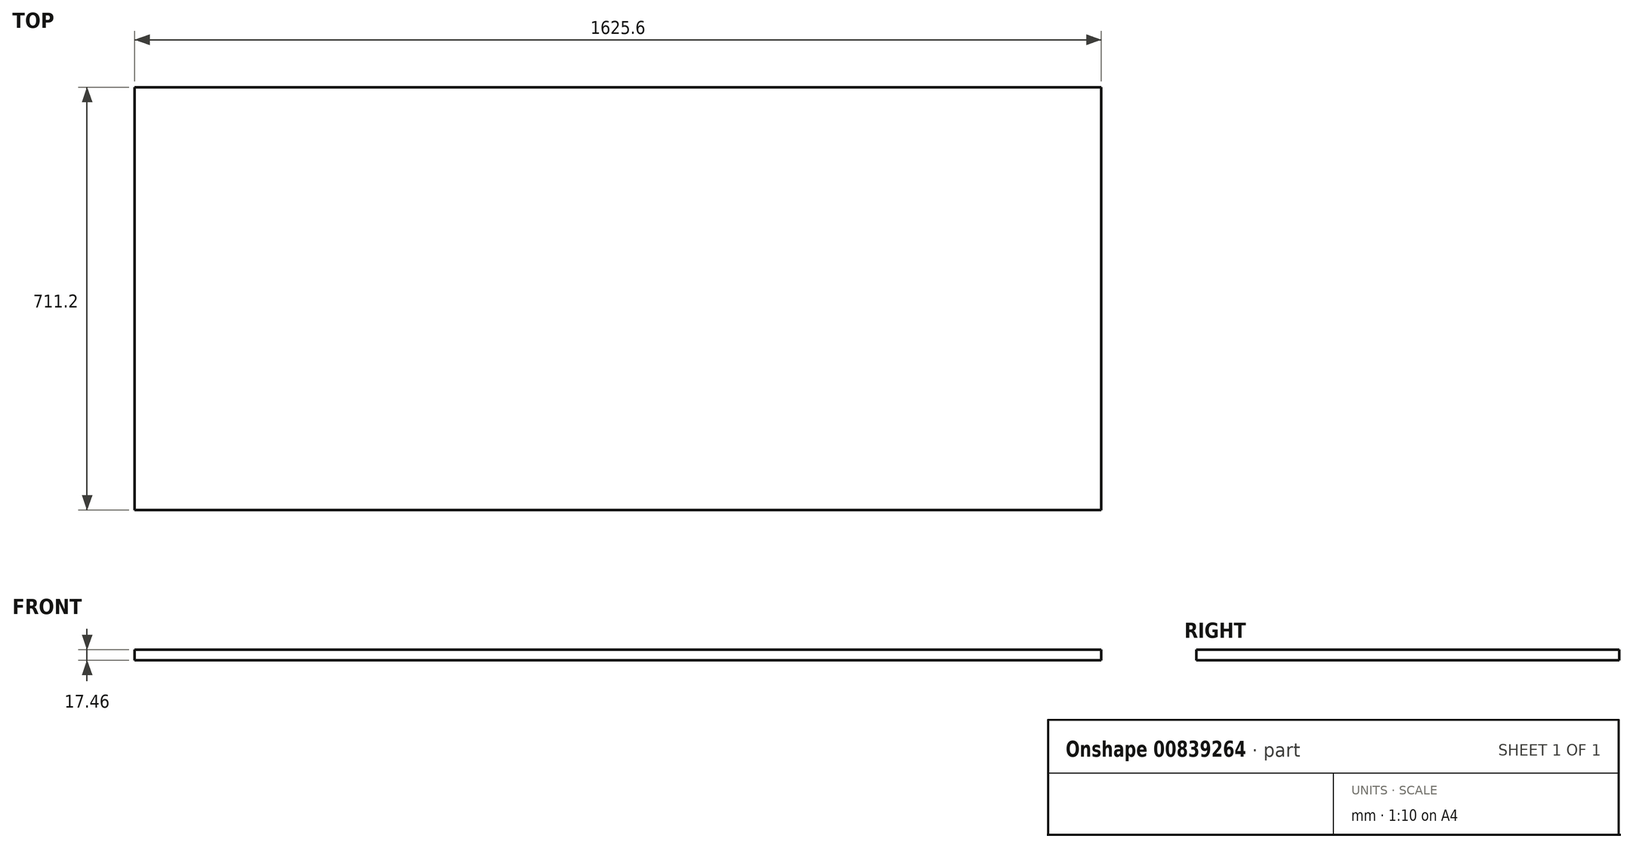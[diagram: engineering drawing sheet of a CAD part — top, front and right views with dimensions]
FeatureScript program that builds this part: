
annotation { "Feature Type Name" : "Feature", "Feature Type Description" : "" }
export const myFeature = defineFeature(function(context is Context, id is Id, definition is map)
    precondition{}
    {
        {
            var Q0;
            Q0=qCreatedBy(makeId("Top.planeOp"),FACE);
            var sketch = newSketch(context, id + "F0", { "sketchPlane" : qUnion([Q0])});
            skLineSegment(sketch, "E0.bottom", {"start": v(-854, 314.74) * mm, "end": v(771.6, 314.74) * mm});
            skLineSegment(sketch, "E0.top", {"start": v(-854, -396.46) * mm, "end": v(771.6, -396.46) * mm});
            skLineSegment(sketch, "E0.left", {"start": v(-854, 314.74) * mm, "end": v(-854, -396.46) * mm});
            skLineSegment(sketch, "E0.right", {"start": v(771.6, 314.74) * mm, "end": v(771.6, -396.46) * mm});
            skSolve(sketch);
        }
        {
            var Q0;
            Q0 = qSketchRegion(id + "F0", true);
            extrude(context, id + "F1", {"entities" : qUnion([Q0]), "depth" : 17.46 * mm, "offsetDistance" : 25.4 * mm});
        }
    });
